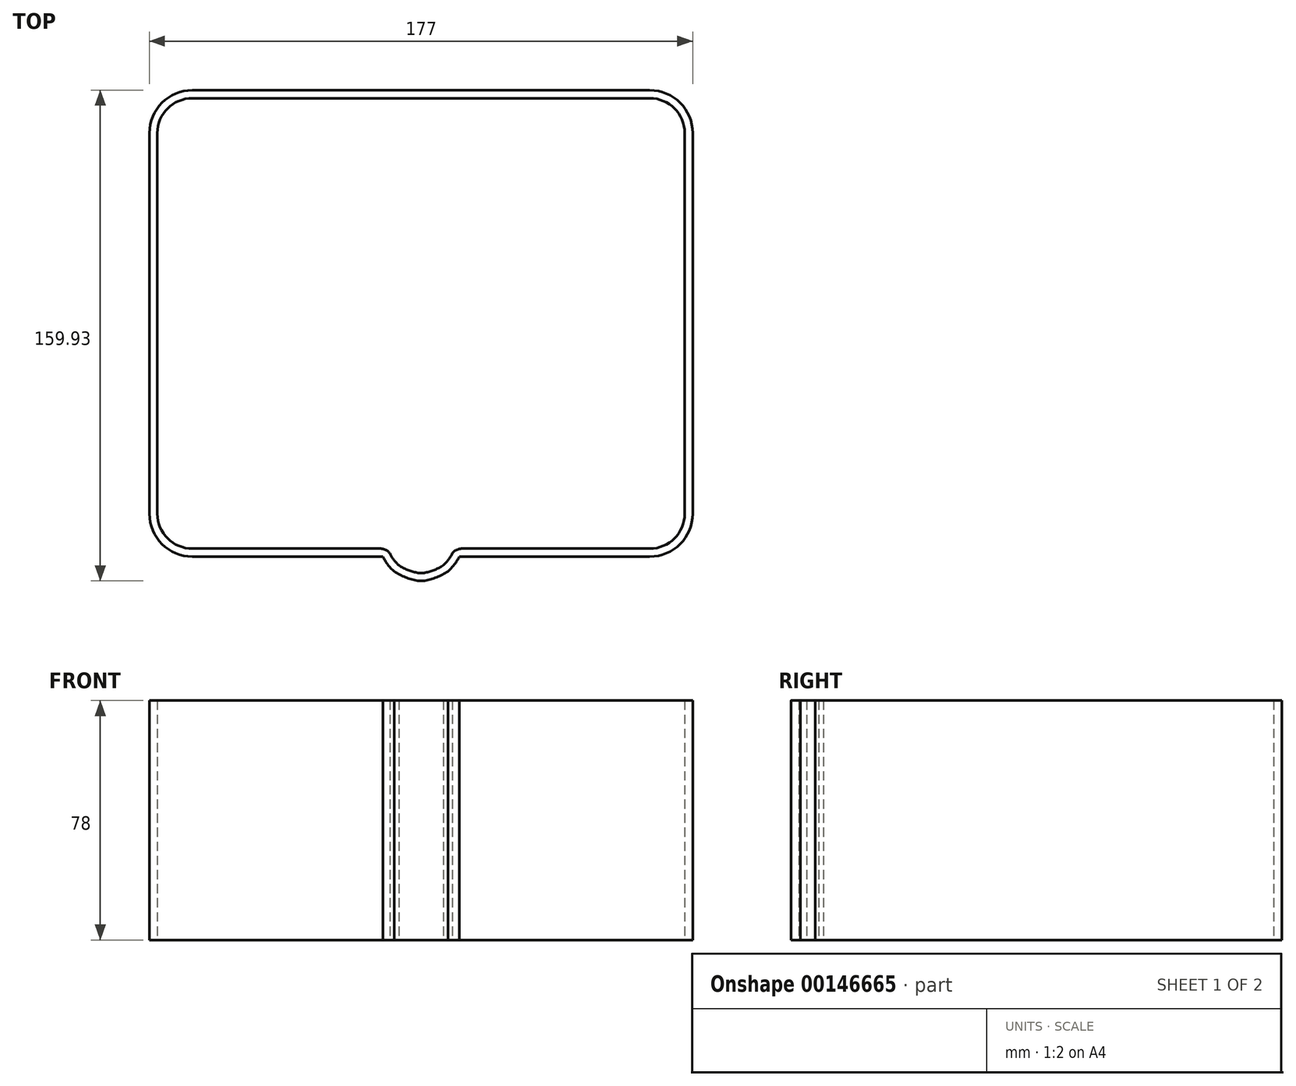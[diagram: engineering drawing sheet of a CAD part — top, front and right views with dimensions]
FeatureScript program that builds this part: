
annotation { "Feature Type Name" : "Feature", "Feature Type Description" : "" }
export const myFeature = defineFeature(function(context is Context, id is Id, definition is map)
    precondition{}
    {
        {
            var Q0;
            Q0=qCreatedBy(makeId("Top.planeOp"),FACE);
            var sketch = newSketch(context, id + "F0", { "sketchPlane" : qUnion([Q0])});
            skLineSegment(sketch, "E0", {"start": v(-142.08, 0) * mm, "end": v(142.08, 0) * mm});
            skPoint(sketch, "E1", {"position": v(0, 0) * mm});
            skSolve(sketch);
        }
        {
            var Q0;
            Q0=qCreatedBy(makeId("Top.planeOp"),FACE);
            var sketch = newSketch(context, id + "F1", { "sketchPlane" : qUnion([Q0])});
            skLineSegment(sketch, "E2.bottom", {"start": v(-74.5, 80.49) * mm, "end": v(0, 80.49) * mm});
            skLineSegment(sketch, "E2.top", {"start": v(-74.5, -71.51) * mm, "end": v(-12.45, -71.51) * mm});
            skLineSegment(sketch, "E2.left", {"start": v(-88.5, 66.49) * mm, "end": v(-88.5, -57.51) * mm});
            skPoint(sketch, "E3.visualSharp", {"position": v(-88.5, 80.49) * mm});
            skArc(sketch, "E3.filletArc", {"start": v(-74.5, 80.49) * mm, "mid": v(-84.4, 76.39) * mm, "end": v(-88.5, 66.49) * mm});
            skPoint(sketch, "E4.visualSharp", {"position": v(-88.5, -71.51) * mm});
            skArc(sketch, "E4.filletArc", {"start": v(-88.5, -57.51) * mm, "mid": v(-84.4, -67.41) * mm, "end": v(-74.5, -71.51) * mm});
            skLineSegment(sketch, "E5.0", {"start": v(-74.5, 77.89) * mm, "end": v(0, 77.89) * mm});
            skArc(sketch, "E5.1", {"start": v(-74.5, 77.89) * mm, "mid": v(-82.56, 74.55) * mm, "end": v(-85.9, 66.49) * mm});
            skLineSegment(sketch, "E5.3", {"start": v(-74.5, -68.91) * mm, "end": v(-13.3, -68.91) * mm});
            skArc(sketch, "E5.4", {"start": v(-85.9, -57.51) * mm, "mid": v(-82.56, -65.57) * mm, "end": v(-74.5, -68.91) * mm});
            skLineSegment(sketch, "E5.5", {"start": v(-85.9, 66.49) * mm, "end": v(-85.9, -57.51) * mm});
            skArc(sketch, "E6", {"start": v(-12.45, -71.51) * mm, "mid": v(-10.84, -74.12) * mm, "end": v(-8.73, -76.34) * mm});
            skArc(sketch, "E7", {"start": v(-8.73, -76.34) * mm, "mid": v(-5.1, -78.25) * mm, "end": v(-1.14, -79.35) * mm});
            skArc(sketch, "E8.2", {"start": v(-7.22, -74.34) * mm, "mid": v(-4.44, -75.82) * mm, "end": v(-1.43, -76.75) * mm});
            skArc(sketch, "E8.3", {"start": v(-10.2, -70.42) * mm, "mid": v(-8.9, -72.53) * mm, "end": v(-7.22, -74.34) * mm});
            skArc(sketch, "E9", {"start": v(-10.2, -70.42) * mm, "mid": v(-11.58, -69.31) * mm, "end": v(-13.3, -68.91) * mm});
            skLineSegment(sketch, "E10", {"start": v(0, -79.5) * mm, "end": v(0, 141.38) * mm, "construction": true});
            skArc(sketch, "E11.MirrorCS", {"start": v(10.2, -70.42) * mm, "mid": v(8.9, -72.53) * mm, "end": v(7.22, -74.34) * mm});
            skArc(sketch, "E12.MirrorCS", {"start": v(10.2, -70.42) * mm, "mid": v(11.58, -69.31) * mm, "end": v(13.3, -68.91) * mm});
            skArc(sketch, "E13.MirrorCS", {"start": v(7.22, -74.34) * mm, "mid": v(4.44, -75.82) * mm, "end": v(1.43, -76.75) * mm});
            skArc(sketch, "E14.MirrorCS", {"start": v(12.45, -71.51) * mm, "mid": v(10.84, -74.12) * mm, "end": v(8.73, -76.34) * mm});
            skLineSegment(sketch, "E15.MirrorCS", {"start": v(74.5, -68.91) * mm, "end": v(13.3, -68.91) * mm});
            skLineSegment(sketch, "E16.MirrorCS", {"start": v(74.5, 80.49) * mm, "end": v(0, 80.49) * mm});
            skPoint(sketch, "E17.MirrorP", {"position": v(88.5, -71.51) * mm});
            skLineSegment(sketch, "E18.MirrorCS", {"start": v(74.5, -71.51) * mm, "end": v(12.45, -71.51) * mm});
            skLineSegment(sketch, "E19.MirrorCS", {"start": v(88.5, 66.49) * mm, "end": v(88.5, -57.51) * mm});
            skArc(sketch, "E20.MirrorCS", {"start": v(85.9, -57.51) * mm, "mid": v(82.56, -65.57) * mm, "end": v(74.5, -68.91) * mm});
            skPoint(sketch, "E21.MirrorP", {"position": v(88.5, 80.49) * mm});
            skArc(sketch, "E22.MirrorCS", {"start": v(74.5, 80.49) * mm, "mid": v(84.4, 76.39) * mm, "end": v(88.5, 66.49) * mm});
            skArc(sketch, "E23.MirrorCS", {"start": v(88.5, -57.51) * mm, "mid": v(84.4, -67.41) * mm, "end": v(74.5, -71.51) * mm});
            skLineSegment(sketch, "E24.MirrorCS", {"start": v(85.9, 66.49) * mm, "end": v(85.9, -57.51) * mm});
            skLineSegment(sketch, "E25.MirrorCS", {"start": v(74.5, 77.89) * mm, "end": v(0, 77.89) * mm});
            skArc(sketch, "E26.MirrorCS", {"start": v(74.5, 77.89) * mm, "mid": v(82.56, 74.55) * mm, "end": v(85.9, 66.49) * mm});
            skArc(sketch, "E27.MirrorCS", {"start": v(8.73, -76.34) * mm, "mid": v(5.1, -78.25) * mm, "end": v(1.14, -79.35) * mm});
            skPoint(sketch, "E28.visualSharp", {"position": v(0, -79.5) * mm});
            skArc(sketch, "E28.filletArc", {"start": v(-1.14, -79.35) * mm, "mid": v(0, -79.44) * mm, "end": v(1.14, -79.35) * mm});
            skPoint(sketch, "E29.visualSharp", {"position": v(0, -76.98) * mm});
            skArc(sketch, "E29.filletArc", {"start": v(-1.43, -76.75) * mm, "mid": v(0, -76.9) * mm, "end": v(1.43, -76.75) * mm});
            skSolve(sketch);
        }
        {
            var Q0;
            Q0 = qSketchRegion(id + "F1", true);
            extrude(context, id + "F2", {"entities" : qUnion([Q0]), "depth" : 78 * mm});
        }
    });
